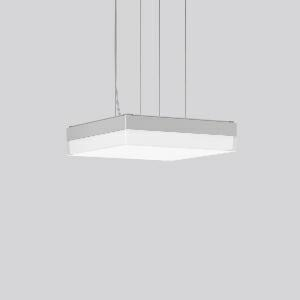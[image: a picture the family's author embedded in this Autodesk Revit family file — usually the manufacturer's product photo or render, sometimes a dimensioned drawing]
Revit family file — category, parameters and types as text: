
# Revit family: flat_slim_square_312542_004_6856
name_source: partatom
category: Lighting Fixtures
units: mm (PartAtom-declared; Revit-internal decimal feet)

## family parameters
Cut with Voids When Loaded = No
Host = Face
Light Source = No
Part Type = Normal
Room Calculation Point = No
Round Connector Dimension = Use Diameter
Shared = No

## types (1)
- MultiLumen 2 840 (1 x LED Modul 840, 2200 lm, 4000)
    Apparent Load = 19 VA
    CIE Flux Codes = 43 75 93 91 100
    Color Rendering = 80
    Color Temperature = 4000
    Default Elevation = 1800 mm
    Height = 70 mm
    Lamp = 1 x LED Modul 840
    Lamp Light Flux = 2200 lm
    Lamp count = 1
    Length = 300 mm
    Lifetime = 50000 h
    Luminous efficacy = 116 lm/W
    Manufacturer = RZB
    ModVariant = No
    Model = 312542.004
    Mounting Place = Ceiling
    Mounting Type = Pendant
    Number of Poles = 1
    OnlyDefault = Yes
    Power Factor = 1
    Product Name = FLAT SLIM square
    Product group = Pendant luminaires
    ProductGroupID = 902
    Protection Class = Protection class I
    Protection Degree = IP 40
    RLX_Detail_Level = 1
    RLX_Emergency_Light_Flux = 0 lm
    RLX_Emergency_Type = 0
    RLX_Emergency_Type_DB = No
    RlxData = <blob elided: 14289 chars, md5=2f3f6be8>
    Socket = socket
    Standby Power = 0 W
    System Light Flux = 2200 lm
    System Power = 19 W
    Type Comments = MultiLumen 2 840
    Type Image = 312542.004.jpg
    URL = http://relux.com
    VarID = multilumen_2_840
    Voltage = 230 V
    Voltage Range = 220-240 V
    Weight = 0.00 kg
    Width = 300 mm

## geometry (parser evidence)
native form markers: Sweep x12
no freeform markers — native parametric forms only
